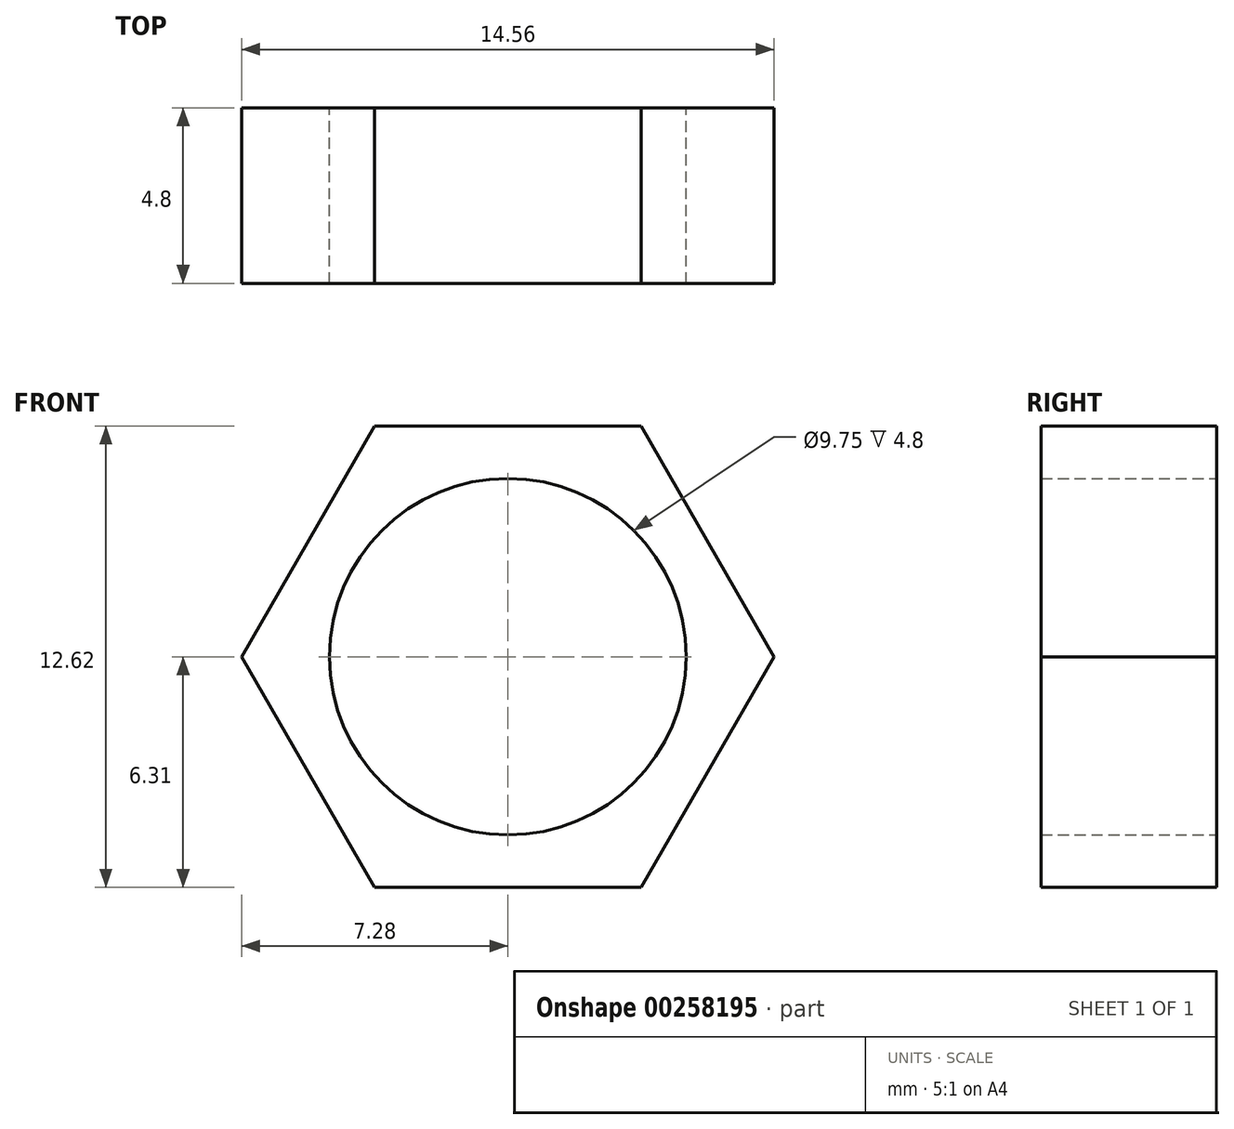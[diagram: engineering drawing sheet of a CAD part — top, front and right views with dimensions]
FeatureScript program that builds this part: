
annotation { "Feature Type Name" : "Feature", "Feature Type Description" : "" }
export const myFeature = defineFeature(function(context is Context, id is Id, definition is map)
    precondition{}
    {
        {
            var Q0;
            Q0=qCreatedBy(makeId("Front.planeOp"),FACE);
            var sketch = newSketch(context, id + "F0", { "sketchPlane" : qUnion([Q0])});
            skCircle(sketch, "E0.cCircle", {"center": v(0, 0) * mm, "radius": 6.3 * mm, "construction": true});
            skLineSegment(sketch, "E0.0", {"start": v(-3.64, 6.3) * mm, "end": v(3.64, 6.3) * mm});
            skLineSegment(sketch, "E0.1", {"start": v(3.64, 6.3) * mm, "end": v(7.28, 0) * mm});
            skLineSegment(sketch, "E0.2", {"start": v(7.28, 0) * mm, "end": v(3.64, -6.3) * mm});
            skLineSegment(sketch, "E0.3", {"start": v(3.64, -6.3) * mm, "end": v(-3.64, -6.3) * mm});
            skLineSegment(sketch, "E0.4", {"start": v(-3.64, -6.3) * mm, "end": v(-7.28, 0) * mm});
            skLineSegment(sketch, "E0.5", {"start": v(-7.28, 0) * mm, "end": v(-3.64, 6.3) * mm});
            skPoint(sketch, "E0.0.midPoint", {"position": v(0, 6.3) * mm});
            skCircle(sketch, "E1", {"center": v(0, 0) * mm, "radius": 4.88 * mm});
            skSolve(sketch);
        }
        {
            var Q0;
            Q0 = qSketchRegion(id + "F0", true);
            extrude(context, id + "F1", {"entities" : qUnion([Q0]), "endBound" : BoundingType.SYMMETRIC, "depth" : 4.8 * mm});
        }
    });
